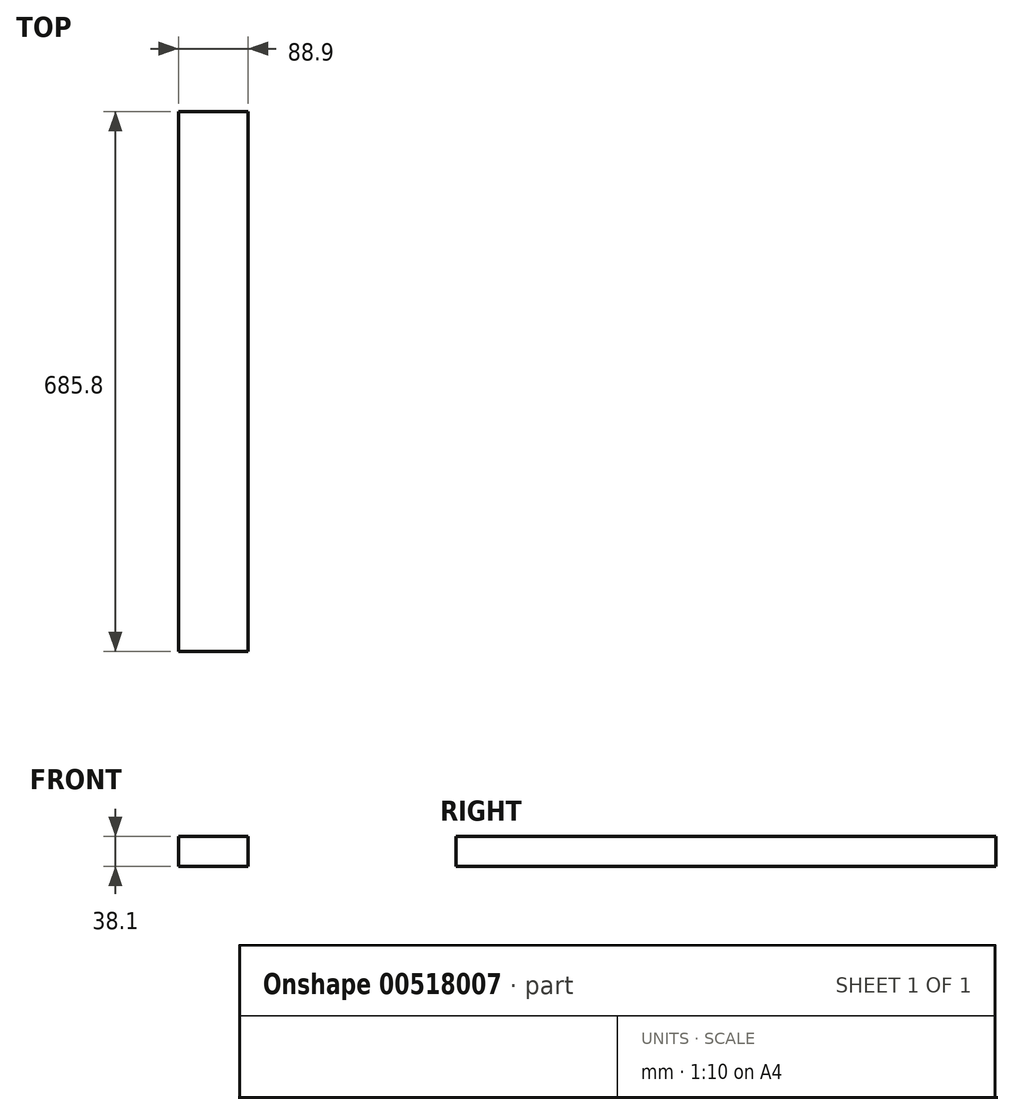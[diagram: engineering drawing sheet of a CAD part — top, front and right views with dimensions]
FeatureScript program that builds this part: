
annotation { "Feature Type Name" : "Feature", "Feature Type Description" : "" }
export const myFeature = defineFeature(function(context is Context, id is Id, definition is map)
    precondition{}
    {
        {
            var Q0;
            Q0=qCreatedBy(makeId("Front.planeOp"),FACE);
            var sketch = newSketch(context, id + "F0", { "sketchPlane" : qUnion([Q0])});
            skLineSegment(sketch, "E0.bottom", {"start": v(0, 0) * mm, "end": v(88.9, 0) * mm});
            skLineSegment(sketch, "E0.top", {"start": v(0, 38.1) * mm, "end": v(88.9, 38.1) * mm});
            skLineSegment(sketch, "E0.left", {"start": v(0, 0) * mm, "end": v(0, 38.1) * mm});
            skLineSegment(sketch, "E0.right", {"start": v(88.9, 0) * mm, "end": v(88.9, 38.1) * mm});
            skSolve(sketch);
        }
        {
            var Q0;
            Q0=qSketchRegion(id+"F0",true);
            extrude(context, id + "F1", {"entities" : qUnion([Q0]), "depth" : 685.8 * mm, "offsetDistance" : 25 * mm});
        }
    });
